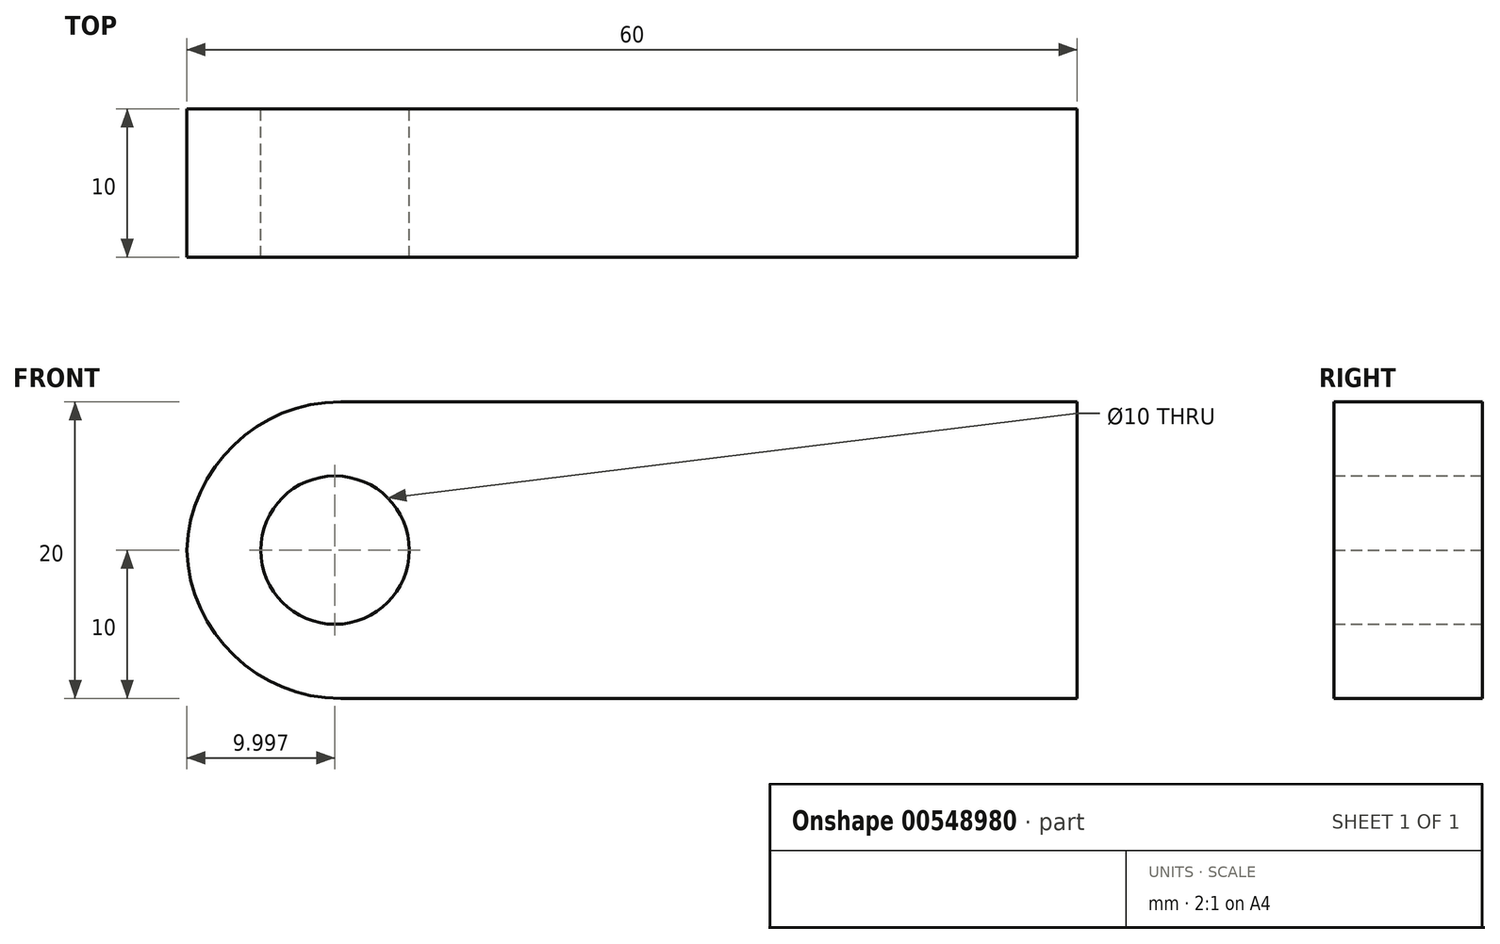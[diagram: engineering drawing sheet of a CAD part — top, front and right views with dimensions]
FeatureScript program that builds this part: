
annotation { "Feature Type Name" : "Feature", "Feature Type Description" : "" }
export const myFeature = defineFeature(function(context is Context, id is Id, definition is map)
    precondition{}
    {
        {
            var Q0;
            Q0=qCreatedBy(makeId("Front.planeOp"),FACE);
            var sketch = newSketch(context, id + "F0", { "sketchPlane" : qUnion([Q0])});
            skLineSegment(sketch, "E0", {"start": v(-34.85, 0) * mm, "end": v(-34.85, 20) * mm});
            skLineSegment(sketch, "E1", {"start": v(-34.85, 20) * mm, "end": v(25.15, 20) * mm});
            skLineSegment(sketch, "E2", {"start": v(25.15, 20) * mm, "end": v(25.15, 0) * mm});
            skLineSegment(sketch, "E3", {"start": v(25.15, 0) * mm, "end": v(-34.85, 0) * mm});
            skLineSegment(sketch, "E4", {"start": v(-34.85, 10) * mm, "end": v(-24.85, 10) * mm});
            skPoint(sketch, "E4.endSnap0", {"position": v(-34.85, 10) * mm});
            skCircle(sketch, "E5", {"center": v(-24.85, 10) * mm, "radius": 5 * mm});
            skSolve(sketch);
        }
        {
            var Q0;
            Q0 = qSketchRegion(id + "F0", true);
            extrude(context, id + "F1", {"entities" : qUnion([Q0]), "depth" : 10 * mm, "offsetDistance" : 25 * mm});
        }
        {
            var Q0;
            Q0=makeQuery(id+"F1.opExtrude","SWEPT_EDGE",EDGE,{"disambiguationData":[OSD([sQuery(id+"F0.wireOp",EDGE,"E0"),sQuery(id+"F0.wireOp",EDGE,"E1")])]});
            var Q1;
            Q1=makeQuery(id+"F1.opExtrude","SWEPT_EDGE",EDGE,{"disambiguationData":[OSD([sQuery(id+"F0.wireOp",EDGE,"E0"),sQuery(id+"F0.wireOp",EDGE,"E3")])]});
            fillet(context, id + "F2", {"entities" : qUnion([Q0, Q1]), "radius" : 10.38 * mm, "tangentPropagation" : true, "allowEdgeOverflow" : false});
        }
    });
